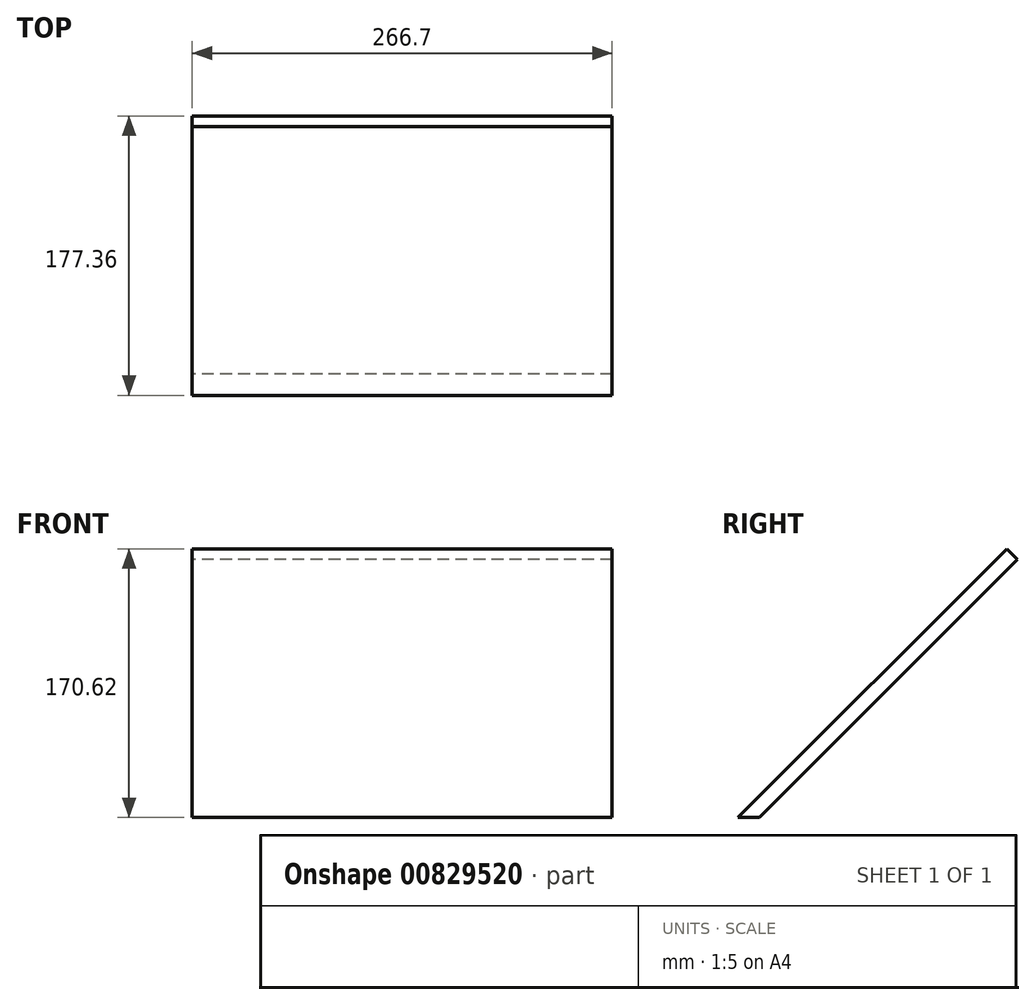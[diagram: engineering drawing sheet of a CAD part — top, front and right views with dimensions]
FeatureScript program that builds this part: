
annotation { "Feature Type Name" : "Feature", "Feature Type Description" : "" }
export const myFeature = defineFeature(function(context is Context, id is Id, definition is map)
    precondition{}
    {
        {
            var Q0;
            Q0=qCreatedBy(makeId("Right.planeOp"),FACE);
            var sketch = newSketch(context, id + "F0", { "sketchPlane" : qUnion([Q0])});
            skLineSegment(sketch, "E0", {"start": v(-143.95, -41.3) * mm, "end": v(26.67, 129.33) * mm});
            skLineSegment(sketch, "E1", {"start": v(-143.95, -41.3) * mm, "end": v(-130.48, -41.3) * mm});
            skLineSegment(sketch, "E2.0", {"start": v(-130.48, -41.3) * mm, "end": v(33.4, 122.6) * mm});
            skLineSegment(sketch, "E3", {"start": v(26.67, 129.33) * mm, "end": v(33.4, 122.6) * mm});
            skSolve(sketch);
        }
        {
            var Q0;
            Q0 = qSketchRegion(id + "F0", true);
            extrude(context, id + "F1", {"entities" : qUnion([Q0]), "depth" : 266.7 * mm, "offsetDistance" : 25.4 * mm});
        }
    });
